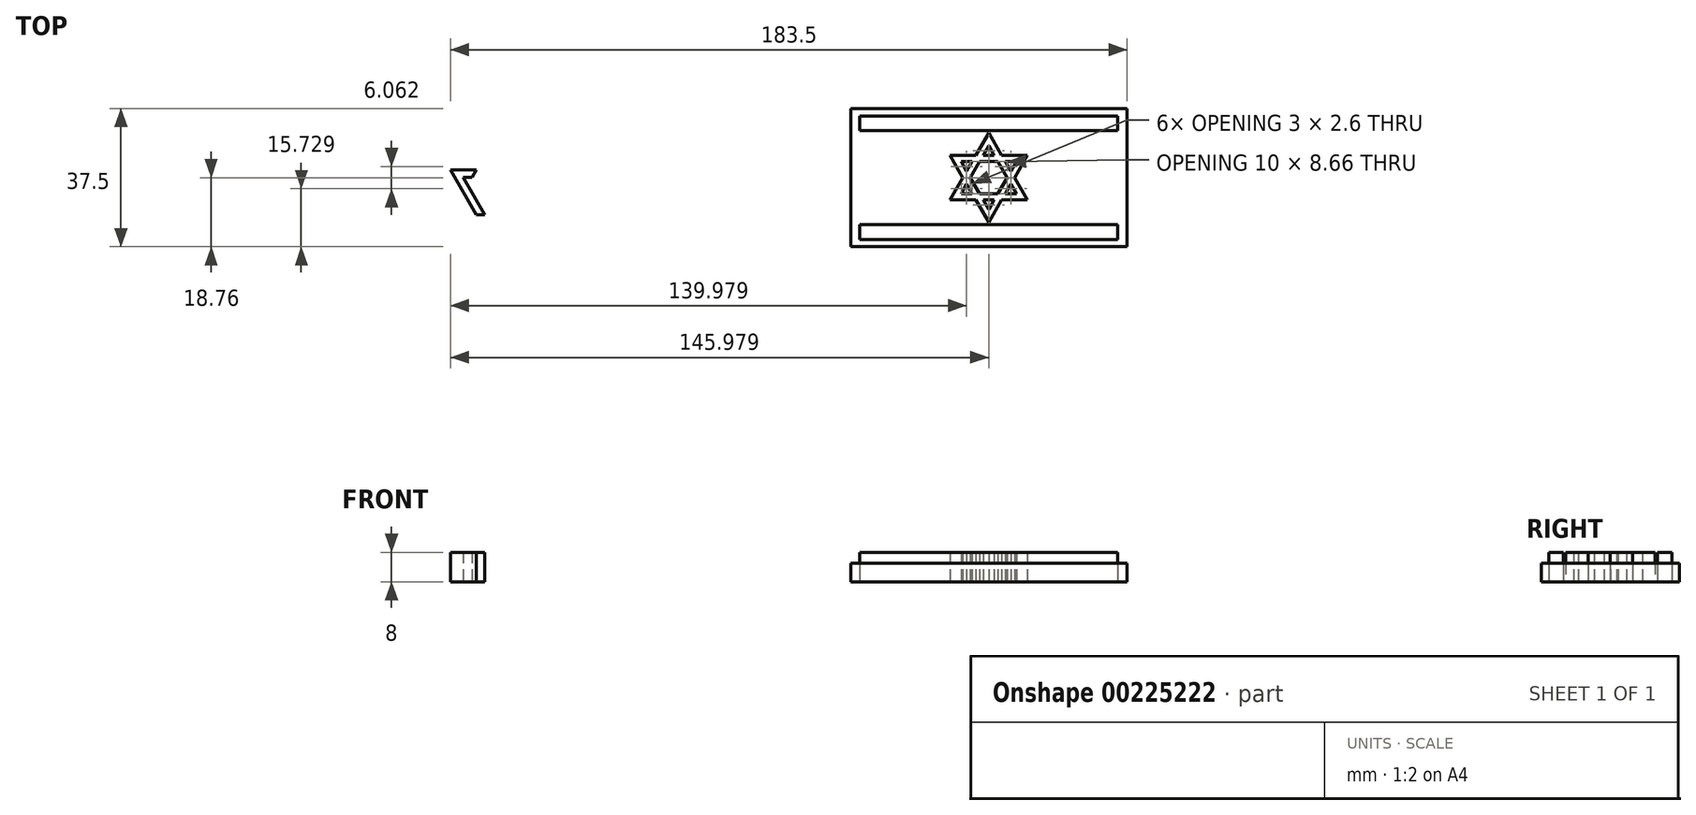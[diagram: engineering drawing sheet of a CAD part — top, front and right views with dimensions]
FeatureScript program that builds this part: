
annotation { "Feature Type Name" : "Feature", "Feature Type Description" : "" }
export const myFeature = defineFeature(function(context is Context, id is Id, definition is map)
    precondition{}
    {
        {
            var Q0;
            Q0=qCreatedBy(makeId("Top.planeOp"),FACE);
            var sketch = newSketch(context, id + "F0", { "sketchPlane" : qUnion([Q0])});
            skLineSegment(sketch, "E0.bottom", {"start": v(-37.5, 18.75) * mm, "end": v(37.5, 18.75) * mm});
            skLineSegment(sketch, "E0.top", {"start": v(-37.5, -18.75) * mm, "end": v(37.5, -18.75) * mm});
            skLineSegment(sketch, "E0.left", {"start": v(-37.5, 18.75) * mm, "end": v(-37.5, -18.75) * mm});
            skLineSegment(sketch, "E0.right", {"start": v(37.5, 18.75) * mm, "end": v(37.5, -18.75) * mm});
            skSolve(sketch);
        }
        {
            var Q0;
            Q0=makeQuery(id+"F0.imprint","IMPRINT",FACE,{"disambiguationData":[TD([[makeQuery(id+"F0.imprint","IMPRINT",EDGE,{"derivedFrom":sQuery(id+"F0.wireOp",EDGE,"E0.bottom")}),-1.0]])]});
            extrude(context, id + "F1", {"entities" : qUnion([Q0]), "depth" : 5 * mm});
        }
        {
            var Q0;
            Q0=qCreatedBy(makeId("Top.planeOp"),FACE);
            var sketch = newSketch(context, id + "F2", { "sketchPlane" : qUnion([Q0])});
            skLineSegment(sketch, "E1.bottom", {"start": v(-35, 16.75) * mm, "end": v(35, 16.75) * mm});
            skLineSegment(sketch, "E1.top", {"start": v(-35, 12.75) * mm, "end": v(35, 12.75) * mm});
            skLineSegment(sketch, "E1.left", {"start": v(-35, 16.75) * mm, "end": v(-35, 12.75) * mm});
            skLineSegment(sketch, "E1.right", {"start": v(35, 16.75) * mm, "end": v(35, 12.75) * mm});
            skLineSegment(sketch, "E2.bottom", {"start": v(-35, -12.75) * mm, "end": v(35, -12.75) * mm});
            skLineSegment(sketch, "E2.top", {"start": v(-35, -16.75) * mm, "end": v(35, -16.75) * mm});
            skLineSegment(sketch, "E2.left", {"start": v(-35, -12.75) * mm, "end": v(-35, -16.75) * mm});
            skLineSegment(sketch, "E2.right", {"start": v(35, -12.75) * mm, "end": v(35, -16.75) * mm});
            skSolve(sketch);
        }
        {
            var Q0;
            Q0=makeQuery(id+"F2.imprint","IMPRINT",FACE,{"disambiguationData":[TD([[makeQuery(id+"F2.imprint","IMPRINT",EDGE,{"derivedFrom":sQuery(id+"F2.wireOp",EDGE,"E1.bottom")}),-1.0]])]});
            var Q1;
            Q1=makeQuery(id+"F2.imprint","IMPRINT",FACE,{"disambiguationData":[TD([[makeQuery(id+"F2.imprint","IMPRINT",EDGE,{"derivedFrom":sQuery(id+"F2.wireOp",EDGE,"E2.bottom")}),-1.0]])]});
            var Q2;
            Q2=sQuery(id+"F0.wireOp",EDGE,"drs8YQxD-VdXT-mpCp-gJ2x-4mLMjrOHQiRa.bottom");
            extrude(context, id + "F3", {"entities" : qUnion([Q0, Q1]), "surfaceEntities" : qUnion([Q2]), "depth" : 8 * mm});
        }
        {
            var Q0;
            Q0=qCreatedBy(makeId("Top.planeOp"),FACE);
            var sketch = newSketch(context, id + "F4", { "sketchPlane" : qUnion([Q0])});
            skLineSegment(sketch, "E3", {"start": v(-10.52, -6.05) * mm, "end": v(-0.02, 12.13) * mm});
            skLineSegment(sketch, "E4", {"start": v(-0.02, 12.13) * mm, "end": v(10.48, -6.05) * mm});
            skLineSegment(sketch, "E5", {"start": v(10.48, -6.05) * mm, "end": v(-10.52, -6.05) * mm});
            skLineSegment(sketch, "E6", {"start": v(10.48, 6.07) * mm, "end": v(-0.02, -12.11) * mm});
            skLineSegment(sketch, "E7", {"start": v(-0.02, -12.11) * mm, "end": v(-10.52, 6.07) * mm});
            skLineSegment(sketch, "E8", {"start": v(-10.52, 6.07) * mm, "end": v(10.48, 6.07) * mm});
            skLineSegment(sketch, "E9", {"start": v(-6.02, -1.72) * mm, "end": v(-7.52, -4.32) * mm});
            skLineSegment(sketch, "E10", {"start": v(-7.52, -4.32) * mm, "end": v(-4.52, -4.32) * mm});
            skLineSegment(sketch, "E11", {"start": v(-4.52, -4.32) * mm, "end": v(-6.02, -1.72) * mm});
            skLineSegment(sketch, "E12", {"start": v(-0.02, -8.65) * mm, "end": v(1.48, -6.05) * mm});
            skLineSegment(sketch, "E13", {"start": v(1.48, -6.05) * mm, "end": v(-1.52, -6.05) * mm});
            skLineSegment(sketch, "E14", {"start": v(-1.52, -6.05) * mm, "end": v(-0.02, -8.65) * mm});
            skLineSegment(sketch, "E15", {"start": v(5.98, -1.72) * mm, "end": v(4.48, -4.32) * mm});
            skLineSegment(sketch, "E16", {"start": v(4.48, -4.32) * mm, "end": v(7.48, -4.32) * mm});
            skLineSegment(sketch, "E17", {"start": v(7.48, -4.32) * mm, "end": v(5.98, -1.72) * mm});
            skLineSegment(sketch, "E18", {"start": v(-0.02, 8.67) * mm, "end": v(-1.52, 6.07) * mm});
            skLineSegment(sketch, "E19", {"start": v(-1.52, 6.07) * mm, "end": v(1.48, 6.07) * mm});
            skLineSegment(sketch, "E20", {"start": v(1.48, 6.07) * mm, "end": v(-0.02, 8.67) * mm});
            skLineSegment(sketch, "E21", {"start": v(-6.02, 1.74) * mm, "end": v(-4.52, 4.34) * mm});
            skLineSegment(sketch, "E22", {"start": v(-4.52, 4.34) * mm, "end": v(-7.52, 4.34) * mm});
            skLineSegment(sketch, "E23", {"start": v(-7.52, 4.34) * mm, "end": v(-6.02, 1.74) * mm});
            skLineSegment(sketch, "E24", {"start": v(5.98, 1.74) * mm, "end": v(7.48, 4.34) * mm});
            skLineSegment(sketch, "E25", {"start": v(7.48, 4.34) * mm, "end": v(4.48, 4.34) * mm});
            skLineSegment(sketch, "E26", {"start": v(4.48, 4.34) * mm, "end": v(1.71, 3.18) * mm});
            skLineSegment(sketch, "E27", {"start": v(-2.52, 4.34) * mm, "end": v(-5.02, 0.01) * mm});
            skLineSegment(sketch, "E28", {"start": v(-5.02, 0.01) * mm, "end": v(-2.52, -4.32) * mm});
            skLineSegment(sketch, "E29", {"start": v(-2.52, -4.32) * mm, "end": v(2.48, -4.32) * mm});
            skLineSegment(sketch, "E30", {"start": v(2.48, -4.32) * mm, "end": v(4.98, 0.01) * mm});
            skLineSegment(sketch, "E31", {"start": v(4.98, 0.01) * mm, "end": v(2.48, 4.34) * mm});
            skLineSegment(sketch, "E32", {"start": v(2.48, 4.34) * mm, "end": v(-2.52, 4.34) * mm});
            skLineSegment(sketch, "E33", {"start": v(7.48, 4.34) * mm, "end": v(-7.52, 4.34) * mm, "construction": true});
            skLineSegment(sketch, "E34", {"start": v(-7.52, 4.34) * mm, "end": v(-0.02, -8.65) * mm, "construction": true});
            skLineSegment(sketch, "E35", {"start": v(-0.02, -8.65) * mm, "end": v(7.48, 4.34) * mm, "construction": true});
            skCircle(sketch, "E36", {"center": v(-0.02, 0.01) * mm, "radius": 12.12 * mm, "construction": true});
            skCircle(sketch, "E37", {"center": v(-0.02, 0.01) * mm, "radius": 8.66 * mm, "construction": true});
            skLineSegment(sketch, "E38", {"start": v(-0.02, 8.67) * mm, "end": v(-7.52, -4.32) * mm, "construction": true});
            skPoint(sketch, "E38.startSnap0", {"position": v(-0.02, 6.07) * mm});
            skLineSegment(sketch, "E39", {"start": v(-7.52, -4.32) * mm, "end": v(7.48, -4.32) * mm, "construction": true});
            skLineSegment(sketch, "E40", {"start": v(7.48, -4.32) * mm, "end": v(-0.02, 8.67) * mm, "construction": true});
            skCircle(sketch, "E41", {"center": v(-0.02, 0.01) * mm, "radius": 5 * mm, "construction": true});
            skLineSegment(sketch, "E42", {"start": v(-146.06, -10.02) * mm, "end": v(-135.56, 8.16) * mm});
            skLineSegment(sketch, "E43", {"start": v(-135.56, 8.16) * mm, "end": v(-125.06, -10.02) * mm});
            skLineSegment(sketch, "E44", {"start": v(-125.06, -10.02) * mm, "end": v(-146.06, -10.02) * mm});
            skLineSegment(sketch, "E45", {"start": v(-125, 2.1) * mm, "end": v(-135.5, -16.08) * mm});
            skLineSegment(sketch, "E46", {"start": v(-135.5, -16.08) * mm, "end": v(-146, 2.1) * mm});
            skLineSegment(sketch, "E47", {"start": v(-146, 2.1) * mm, "end": v(-125, 2.1) * mm});
            skLineSegment(sketch, "E48", {"start": v(-142.42, -8) * mm, "end": v(-135.42, 4.13) * mm});
            skLineSegment(sketch, "E49", {"start": v(-135.42, 4.13) * mm, "end": v(-128.42, -8) * mm});
            skLineSegment(sketch, "E50", {"start": v(-128.42, -8) * mm, "end": v(-142.42, -8) * mm});
            skLineSegment(sketch, "E51", {"start": v(-128.56, 0.08) * mm, "end": v(-135.56, -12.04) * mm});
            skLineSegment(sketch, "E52", {"start": v(-135.56, -12.04) * mm, "end": v(-142.56, 0.08) * mm});
            skLineSegment(sketch, "E53", {"start": v(-142.56, 0.08) * mm, "end": v(-128.56, 0.08) * mm});
            skCircle(sketch, "E54", {"center": v(-135.56, -3.96) * mm, "radius": 12.12 * mm, "construction": true});
            skCircle(sketch, "E55", {"center": v(-135.56, -3.96) * mm, "radius": 8.08 * mm, "construction": true});
            skSolve(sketch);
        }
        {
            var Q0;
            Q0=makeQuery(id+"F4.imprint","IMPRINT",FACE,{"disambiguationData":[TD([[makeQuery(id+"F4.imprint","IMPRINT",EDGE,{"derivedFrom":sQuery(id+"F4.wireOp",EDGE,"E27")}),-1.0]])]});
            var Q1;
            Q1=makeQuery(id+"F4.imprint","IMPRINT",FACE,{"disambiguationData":[TD([[makeQuery(id+"F4.imprint","IMPRINT",EDGE,{"derivedFrom":sQuery(id+"F4.wireOp",EDGE,"E9")}),-1.0]])]});
            var Q2;
            Q2=makeQuery(id+"F4.imprint","IMPRINT",FACE,{"disambiguationData":[TD([[makeQuery(id+"F4.imprint","IMPRINT",EDGE,{"derivedFrom":sQuery(id+"F4.wireOp",EDGE,"E21")}),-1.0]])]});
            var Q3;
            Q3=makeQuery(id+"F4.imprint","IMPRINT",FACE,{"disambiguationData":[TD([[makeQuery(id+"F4.imprint","IMPRINT",EDGE,{"derivedFrom":sQuery(id+"F4.wireOp",EDGE,"E18")}),-1.0]])]});
            var Q4;
            Q4=makeQuery(id+"F4.imprint","IMPRINT",FACE,{"disambiguationData":[TD([[makeQuery(id+"F4.imprint","IMPRINT",EDGE,{"derivedFrom":sQuery(id+"F4.wireOp",EDGE,"E24")}),-1.0]])]});
            var Q5;
            Q5=makeQuery(id+"F4.imprint","IMPRINT",FACE,{"disambiguationData":[TD([[makeQuery(id+"F4.imprint","IMPRINT",EDGE,{"derivedFrom":sQuery(id+"F4.wireOp",EDGE,"E15")}),-1.0]])]});
            var Q6;
            Q6=makeQuery(id+"F4.imprint","IMPRINT",FACE,{"disambiguationData":[TD([[makeQuery(id+"F4.imprint","IMPRINT",EDGE,{"derivedFrom":sQuery(id+"F4.wireOp",EDGE,"E12")}),-1.0]])]});
            var Q7;
            {var subQ8=sQuery(id+"F4.wireOp",EDGE,"E22");Q7=makeQuery(id+"F4.imprint","IMPRINT",FACE,{"disambiguationData":[TD([[makeQuery(id+"F4.imprint","IMPRINT",EDGE,{"derivedFrom":subQ8}),-1.0]])]});}
            var Q8;
            {var subQ3=sQuery(id+"F4.wireOp",EDGE,"E5");var subQ5=sQuery(id+"F4.wireOp",EDGE,"E4");var subQ9=makeQuery(id+"F4.imprint","INTERSECT",VERTEX,{"derivedFrom":[subQ5,subQ3]});Q8=makeQuery(id+"F4.imprint","IMPRINT",FACE,{"disambiguationData":[TD([[makeQuery(id+"F4.imprint","IMPRINT",EDGE,{"disambiguationData":[TD([[subQ9,1.0]])],"derivedFrom":subQ5}),-1.0]])]});}
            var Q9;
            {var subQ1=sQuery(id+"F4.wireOp",EDGE,"E46");var subQ3=sQuery(id+"F4.wireOp",EDGE,"E42");var subQ5=makeQuery(id+"F4.imprint","INTERSECT",VERTEX,{"derivedFrom":[subQ3,subQ1]});Q9=makeQuery(id+"F4.imprint","IMPRINT",FACE,{"disambiguationData":[TD([[makeQuery(id+"F4.imprint","IMPRINT",EDGE,{"disambiguationData":[TD([[subQ5,-1.0]])],"derivedFrom":subQ3}),1.0]])]});}
            var Q10;
            {var subQ0=sQuery(id+"F4.wireOp",EDGE,"E46");var subQ1=sQuery(id+"F4.wireOp",EDGE,"E42");var subQ2=makeQuery(id+"F4.imprint","INTERSECT",VERTEX,{"derivedFrom":[subQ1,subQ0]});Q10=makeQuery(id+"F4.imprint","IMPRINT",FACE,{"disambiguationData":[TD([[makeQuery(id+"F4.imprint","IMPRINT",EDGE,{"disambiguationData":[TD([[subQ2,-1.0]])],"derivedFrom":subQ1}),-1.0]])]});}
            var Q11;
            {var subQ0=sQuery(id+"F4.wireOp",EDGE,"E50");var subQ1=sQuery(id+"F4.wireOp",EDGE,"E46");var subQ2=makeQuery(id+"F4.imprint","INTERSECT",VERTEX,{"derivedFrom":[subQ1,subQ0]});Q11=makeQuery(id+"F4.imprint","IMPRINT",FACE,{"disambiguationData":[TD([[makeQuery(id+"F4.imprint","IMPRINT",EDGE,{"disambiguationData":[TD([[subQ2,-1.0]])],"derivedFrom":subQ1}),-1.0]])]});}
            var Q12;
            {var subQ0=sQuery(id+"F4.wireOp",EDGE,"E46");var subQ1=sQuery(id+"F4.wireOp",EDGE,"E44");var subQ2=makeQuery(id+"F4.imprint","INTERSECT",VERTEX,{"derivedFrom":[subQ1,subQ0]});Q12=makeQuery(id+"F4.imprint","IMPRINT",FACE,{"disambiguationData":[TD([[makeQuery(id+"F4.imprint","IMPRINT",EDGE,{"disambiguationData":[TD([[subQ2,1.0]])],"derivedFrom":subQ1}),-1.0]])]});}
            extrude(context, id + "F5", {"entities" : qUnion([Q0, Q1, Q2, Q3, Q4, Q5, Q6, Q7, Q8, Q9, Q10, Q11, Q12]), "depth" : 8 * mm});
        }
    });
